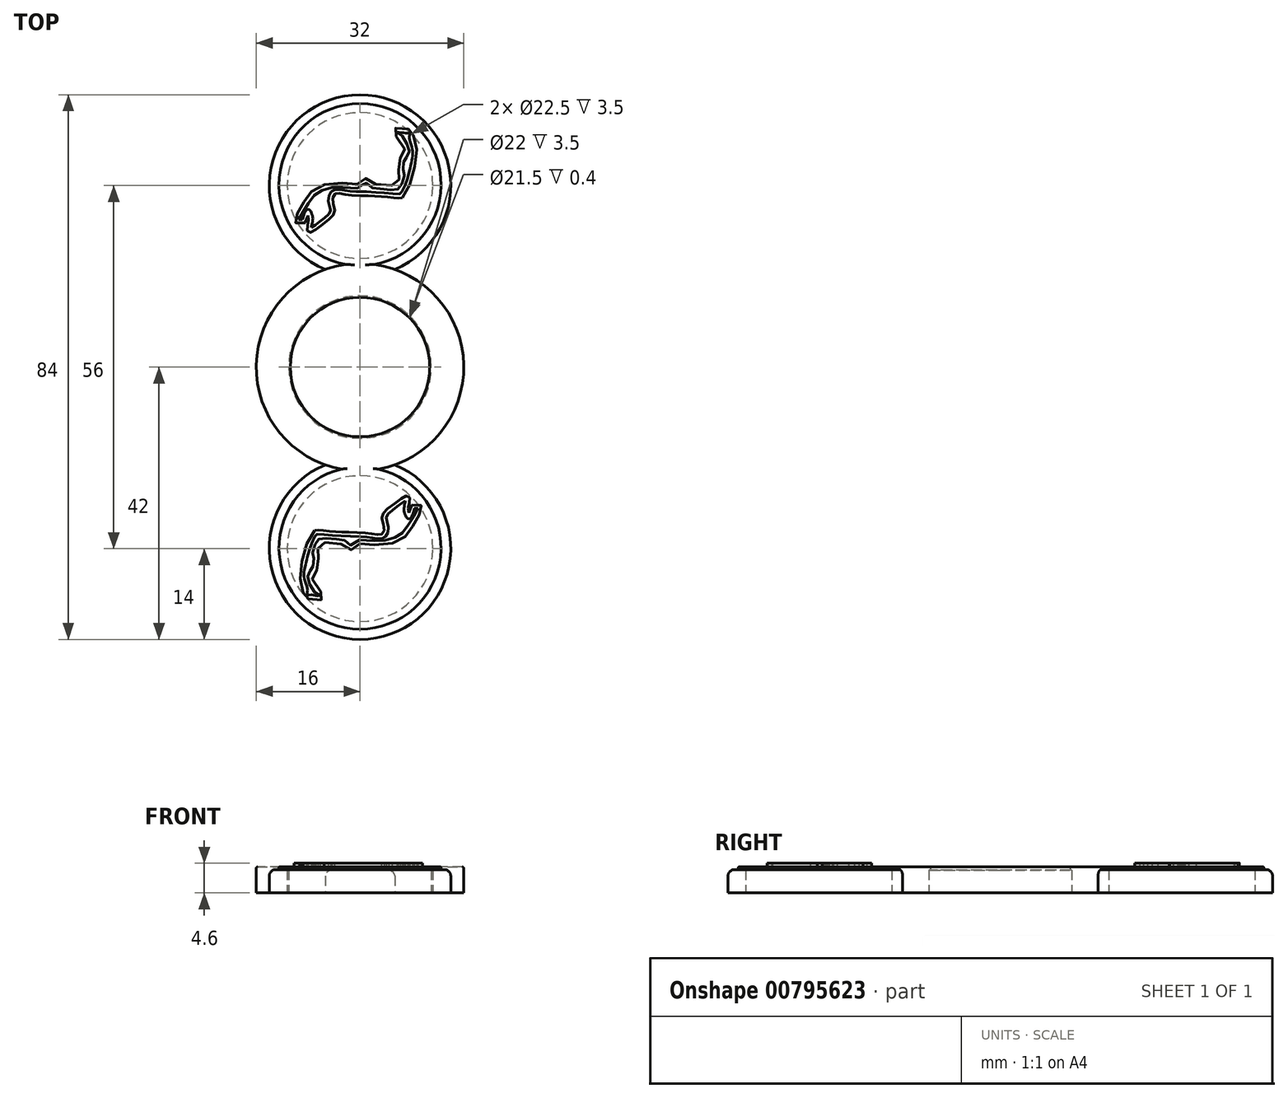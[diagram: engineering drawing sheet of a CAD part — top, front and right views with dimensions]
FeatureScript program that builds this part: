
annotation { "Feature Type Name" : "Feature", "Feature Type Description" : "" }
export const myFeature = defineFeature(function(context is Context, id is Id, definition is map)
    precondition{}
    {
        {
            var Q0;
            Q0=qCreatedBy(makeId("Top.planeOp"),FACE);
            var sketch = newSketch(context, id + "F0", { "sketchPlane" : qUnion([Q0])});
            skCircle(sketch, "E0", {"center": v(0, 0) * mm, "radius": 16 * mm});
            skCircle(sketch, "E1", {"center": v(0, 0) * mm, "radius": 11 * mm});
            skCircle(sketch, "E2", {"center": v(0, 0) * mm, "radius": 10.75 * mm});
            skCircle(sketch, "E3", {"center": v(0, 28) * mm, "radius": 14 * mm});
            skCircle(sketch, "E4", {"center": v(0, 28) * mm, "radius": 11.25 * mm});
            skCircle(sketch, "E5", {"center": v(0, 0) * mm, "radius": 40 * mm, "construction": true});
            skCircle(sketch, "E6", {"center": v(0, -28) * mm, "radius": 14 * mm});
            skCircle(sketch, "E7", {"center": v(0, -28) * mm, "radius": 11.25 * mm});
            skSolve(sketch);
        }
        {
            var Q0;
            Q0=makeQuery(id+"F0.imprint","IMPRINT",FACE,{"disambiguationData":[TD([[makeQuery(id+"F0.imprint","IMPRINT",EDGE,{"derivedFrom":sQuery(id+"F0.wireOp",EDGE,"E1")}),-1.0]])]});
            var Q1;
            {var subQ0=sQuery(id+"F0.wireOp",EDGE,"E3");var subQ1=sQuery(id+"F0.wireOp",EDGE,"E0");var subQ2=makeQuery(id+"F0.imprint","INTERSECT",VERTEX,{"disambiguationData":[OD(0.0)],"derivedFrom":[subQ1,subQ0]});Q1=makeQuery(id+"F0.imprint","IMPRINT",FACE,{"disambiguationData":[TD([[makeQuery(id+"F0.imprint","IMPRINT",EDGE,{"disambiguationData":[TD([[subQ2,1.0]])],"derivedFrom":subQ1}),1.0]])]});}
            var Q2;
            {var subQ0=sQuery(id+"F0.wireOp",EDGE,"E6");var subQ1=sQuery(id+"F0.wireOp",EDGE,"E0");var subQ2=makeQuery(id+"F0.imprint","INTERSECT",VERTEX,{"disambiguationData":[OD(0.0)],"derivedFrom":[subQ1,subQ0]});Q2=makeQuery(id+"F0.imprint","IMPRINT",FACE,{"disambiguationData":[TD([[makeQuery(id+"F0.imprint","IMPRINT",EDGE,{"disambiguationData":[TD([[subQ2,-1.0]])],"derivedFrom":subQ1}),1.0]])]});}
            extrude(context, id + "F1", {"entities" : qUnion([Q0, Q1, Q2]), "depth" : 4 * mm, "offsetDistance" : 25 * mm});
        }
        {
            var Q0;
            Q0=makeQuery(id+"F0.imprint","IMPRINT",FACE,{"disambiguationData":[TD([[makeQuery(id+"F0.imprint","IMPRINT",EDGE,{"derivedFrom":sQuery(id+"F0.wireOp",EDGE,"E1")}),1.0]])]});
            extrude(context, id + "F2", {"entities" : qUnion([Q0]), "operationType" : NewBodyOperationType.ADD, "depth" : 4 * mm, "offsetDistance" : 25 * mm, "hasSecondDirection" : true, "secondDirectionOppositeDirection" : false, "secondDirectionDepth" : 3.5 * mm});
        }
        {
            var Q0;
            Q0=makeQuery(id+"F2.opExtrude","CAP_EDGE",EDGE,{"disambiguationData":[OSD([sQuery(id+"F0.wireOp",EDGE,"E1")])],"isStart":true});
            var Q1;
            Q1=makeQuery(id+"F2.opExtrude","CAP_EDGE",EDGE,{"disambiguationData":[OSD([sQuery(id+"F0.wireOp",EDGE,"E2")])],"isStart":false});
            fillet(context, id + "F3", {"entities" : qUnion([Q0, Q1]), "radius" : 0.1 * mm, "tangentPropagation" : true, "allowEdgeOverflow" : false});
        }
        {
            var Q0;
            Q0=makeQuery(id+"F0.imprint","IMPRINT",FACE,{"disambiguationData":[TD([[makeQuery(id+"F0.imprint","IMPRINT",EDGE,{"derivedFrom":sQuery(id+"F0.wireOp",EDGE,"E7")}),-1.0]])]});
            var Q1;
            Q1=makeQuery(id+"F0.imprint","IMPRINT",FACE,{"disambiguationData":[TD([[makeQuery(id+"F0.imprint","IMPRINT",EDGE,{"derivedFrom":sQuery(id+"F0.wireOp",EDGE,"E4")}),-1.0]])]});
            extrude(context, id + "F4", {"entities" : qUnion([Q0, Q1]), "operationType" : NewBodyOperationType.ADD, "depth" : 3.6 * mm, "offsetDistance" : 25 * mm});
        }
        {
            var Q0;
            Q0=qCreatedBy(makeId("Top.planeOp"),FACE);
            var sketch = newSketch(context, id + "F5", { "sketchPlane" : qUnion([Q0])});
            skCircle(sketch, "E8", {"center": v(0, 28.15) * mm, "radius": 12.5 * mm});
            skCircle(sketch, "E9", {"center": v(0, -27.9) * mm, "radius": 12.5 * mm});
            skSolve(sketch);
        }
        {
            var Q0;
            Q0=makeQuery(id+"F5.imprint","IMPRINT",FACE,{"disambiguationData":[TD([[makeQuery(id+"F5.imprint","IMPRINT",EDGE,{"derivedFrom":sQuery(id+"F5.wireOp",EDGE,"E8")}),1.0]])]});
            var Q1;
            Q1=makeQuery(id+"F5.imprint","IMPRINT",FACE,{"disambiguationData":[TD([[makeQuery(id+"F5.imprint","IMPRINT",EDGE,{"derivedFrom":sQuery(id+"F5.wireOp",EDGE,"E9")}),1.0]])]});
            extrude(context, id + "F6", {"entities" : qUnion([Q0, Q1]), "operationType" : NewBodyOperationType.ADD, "depth" : 4 * mm, "offsetDistance" : 25 * mm, "hasSecondDirection" : true, "secondDirectionOppositeDirection" : false, "secondDirectionDepth" : 3.5 * mm});
        }
        {
            var Q0;
            Q0=makeQuery(id+"F6.boolean.opBoolean","SPLIT",EDGE,{"disambiguationData":[OD(0.0)],"derivedFrom":makeQuery(id+"F1.opExtrude","CAP_EDGE",EDGE,{"disambiguationData":[OSD([sQuery(id+"F0.wireOp",EDGE,"E0")])],"isStart":false})});
            var Q1;
            Q1=makeQuery(id+"F6.boolean.opBoolean","SPLIT",EDGE,{"disambiguationData":[OD(1.0)],"derivedFrom":makeQuery(id+"F1.opExtrude","CAP_EDGE",EDGE,{"disambiguationData":[OSD([sQuery(id+"F0.wireOp",EDGE,"E0")])],"isStart":false})});
            fillet(context, id + "F7", {"entities" : qUnion([Q0, Q1]), "radius" : 0.2 * mm, "tangentPropagation" : true, "allowEdgeOverflow" : false});
        }
        {
            var Q0;
            Q0=makeQuery(id+"F6.boolean.opBoolean","INTERSECT",EDGE,{"derivedFrom":[makeQuery(id+"F4.opExtrude","CAP_FACE",FACE,{"disambiguationData":[OSD([sQuery(id+"F0.wireOp",EDGE,"E0"),sQuery(id+"F0.wireOp",EDGE,"E6"),sQuery(id+"F0.wireOp",EDGE,"E7")])],"isStart":false}),makeQuery(id+"F6.opExtrude","SWEPT_FACE",FACE,{"disambiguationData":[OSD([sQuery(id+"F5.wireOp",EDGE,"E9")])]})]});
            var Q1;
            Q1=makeQuery(id+"F6.boolean.opBoolean","INTERSECT",EDGE,{"derivedFrom":[makeQuery(id+"F4.opExtrude","CAP_FACE",FACE,{"disambiguationData":[OSD([sQuery(id+"F0.wireOp",EDGE,"E0"),sQuery(id+"F0.wireOp",EDGE,"E3"),sQuery(id+"F0.wireOp",EDGE,"E4")])],"isStart":false}),makeQuery(id+"F6.opExtrude","SWEPT_FACE",FACE,{"disambiguationData":[OSD([sQuery(id+"F5.wireOp",EDGE,"E8")])]})]});
            fillet(context, id + "F8", {"entities" : qUnion([Q0, Q1]), "radius" : 0.2 * mm, "tangentPropagation" : true, "allowEdgeOverflow" : false});
        }
        {
            var Q0;
            Q0=makeQuery(id+"F4.opExtrude","CAP_EDGE",EDGE,{"disambiguationData":[OSD([sQuery(id+"F0.wireOp",EDGE,"E3")])],"isStart":false});
            var Q1;
            Q1=makeQuery(id+"F4.opExtrude","CAP_EDGE",EDGE,{"disambiguationData":[OSD([sQuery(id+"F0.wireOp",EDGE,"E6")])],"isStart":false});
            fillet(context, id + "F9", {"entities" : qUnion([Q0, Q1]), "radius" : 1 * mm, "tangentPropagation" : true, "allowEdgeOverflow" : false});
        }
        {
            var Q0;
            Q0=makeQuery(id+"F6.opExtrude","CAP_EDGE",EDGE,{"disambiguationData":[OSD([sQuery(id+"F5.wireOp",EDGE,"E8")])],"isStart":false});
            var Q1;
            Q1=makeQuery(id+"F6.opExtrude","CAP_EDGE",EDGE,{"disambiguationData":[OSD([sQuery(id+"F5.wireOp",EDGE,"E9")])],"isStart":false});
            fillet(context, id + "F10", {"entities" : qUnion([Q0, Q1]), "radius" : 0.1 * mm, "tangentPropagation" : true, "allowEdgeOverflow" : false});
        }
        {
            var Q0;
            Q0=qCreatedBy(makeId("Top.planeOp"),FACE);
            cPlane(context, id + "F11", {"entities" : qUnion([Q0]), "cplaneType" : CPlaneType.OFFSET, "offset" : 3.6 * mm, "width" : 150 * mm, "height" : 150 * mm});
        }
        {
            var Q0;
            Q0=qCreatedBy(id+"F11.planeOp",FACE);
            var sketch = newSketch(context, id + "F12", { "sketchPlane" : qUnion([Q0])});
            skFitSpline(sketch, "E10", {"points": [v(-7.02, -25.2) * mm, v(-6.88, -25.17) * mm, v(-6.76, -25.15) * mm, v(-6.56, -25.14) * mm, v(-6.38, -25.14) * mm, v(-6.2, -25.18) * mm, v(-5.94, -25.2) * mm, v(-5.64, -25.22) * mm, v(-5.24, -25.25) * mm, v(-4.89, -25.28) * mm, v(-4.45, -25.32) * mm, v(-4.06, -25.35) * mm, v(-3.66, -25.37) * mm, v(-3.22, -25.4) * mm, v(-2.82, -25.43) * mm, v(-2.42, -25.46) * mm, v(-1.92, -25.47) * mm, v(-1.37, -25.5) * mm, v(-0.61, -25.53) * mm, v(0.27, -25.54) * mm, v(0.81, -25.57) * mm, v(1.23, -25.61) * mm, v(1.64, -25.69) * mm, v(2.06, -25.73) * mm, v(2.43, -25.8) * mm, v(2.74, -25.87) * mm, v(2.94, -25.87) * mm, v(3.1, -25.86) * mm, v(3.28, -25.82) * mm, v(3.47, -25.72) * mm, v(3.58, -25.54) * mm, v(3.7, -25.32) * mm, v(3.77, -24.95) * mm, v(3.76, -24.57) * mm, v(3.6, -24.12) * mm, v(3.46, -23.76) * mm, v(3.39, -23.37) * mm, v(3.41, -23.12) * mm, v(3.5, -22.81) * mm, v(3.63, -22.5) * mm, v(3.76, -22.31) * mm, v(4, -22.07) * mm, v(4.49, -21.67) * mm, v(5.1, -21.22) * mm, v(5.7, -20.74) * mm, v(6.22, -20.36) * mm, v(6.74, -20.02) * mm, v(6.98, -19.9) * mm, v(7.17, -19.84) * mm, v(7.34, -19.84) * mm, v(7.5, -19.91) * mm, v(7.63, -20.08) * mm, v(7.7, -20.24) * mm, v(7.68, -20.51) * mm, v(7.6, -20.85) * mm, v(7.55, -21.15) * mm, v(7.48, -21.46) * mm, v(7.44, -21.75) * mm, v(7.42, -22.02) * mm, v(7.45, -22.33) * mm, v(7.53, -22.48) * mm], "startDerivative": vector(12.87, 4) * mm, "endDerivative": vector(8.17, -11.49) * mm});
            skFitSpline(sketch, "E11", {"points": [v(7.53, -22.48) * mm, v(7.62, -22.28) * mm, v(7.67, -22.1) * mm, v(7.71, -21.87) * mm, v(7.77, -21.65) * mm, v(7.86, -21.47) * mm, v(7.96, -21.35) * mm, v(8.11, -21.23) * mm, v(8.33, -21.2) * mm, v(8.62, -21.18) * mm, v(8.93, -21.2) * mm, v(9.21, -21.2) * mm, v(9.4, -21.3) * mm, v(9.53, -21.43) * mm, v(9.64, -21.59) * mm, v(9.64, -21.8) * mm, v(9.53, -22.09) * mm, v(9.32, -22.48) * mm, v(9.06, -22.98) * mm, v(8.81, -23.4) * mm, v(8.55, -23.86) * mm, v(8.34, -24.2) * mm, v(8.1, -24.61) * mm, v(7.87, -24.99) * mm, v(7.53, -25.52) * mm, v(7.32, -25.77) * mm, v(7.04, -26.07) * mm, v(6.6, -26.42) * mm, v(6.03, -26.79) * mm, v(5.54, -27) * mm, v(4.91, -27.2) * mm, v(4.22, -27.32) * mm, v(3.17, -27.41) * mm, v(2.14, -27.44) * mm, v(1.35, -27.4) * mm, v(0.67, -27.26) * mm, v(0.23, -27.23) * mm, v(-0.13, -27.28) * mm, v(-0.32, -27.45) * mm, v(-0.51, -27.74) * mm, v(-0.7, -27.96) * mm, v(-0.97, -28.14) * mm, v(-1.46, -28.16) * mm, v(-1.86, -27.93) * mm, v(-2.13, -27.66) * mm, v(-2.47, -27.4) * mm, v(-2.82, -27.3) * mm, v(-3.22, -27.25) * mm, v(-4, -27.17) * mm, v(-4.8, -27.11) * mm, v(-5.52, -27.05) * mm, v(-5.86, -27.03) * mm, v(-5.99, -27.06) * mm, v(-6.1, -27.16) * mm, v(-6.24, -27.37) * mm, v(-6.46, -27.89) * mm, v(-6.64, -28.4) * mm, v(-6.74, -28.78) * mm, v(-6.7, -28.97) * mm, v(-6.57, -29.18) * mm, v(-6.46, -29.38) * mm, v(-6.42, -29.63) * mm, v(-6.48, -30.12) * mm, v(-6.58, -30.56) * mm, v(-6.62, -31.03) * mm, v(-6.67, -31.33) * mm, v(-6.81, -31.64) * mm, v(-7.08, -31.86) * mm, v(-7.33, -32.02) * mm, v(-7.43, -32.13) * mm, v(-7.44, -32.42) * mm, v(-7.2, -33.1) * mm, v(-6.9, -33.83) * mm, v(-6.56, -34.3) * mm, v(-6, -34.69) * mm, v(-5.66, -34.97) * mm, v(-5.53, -35.2) * mm, v(-5.57, -35.57) * mm, v(-5.75, -35.8) * mm, v(-6.04, -35.94) * mm, v(-6.64, -35.94) * mm, v(-7.14, -35.84) * mm, v(-7.58, -35.76) * mm, v(-7.92, -35.76) * mm, v(-8.38, -35.75) * mm, v(-8.6, -35.67) * mm, v(-8.73, -35.52) * mm, v(-8.83, -35.24) * mm, v(-8.8, -34.93) * mm, v(-8.73, -34.64) * mm, v(-8.7, -34.4) * mm, v(-8.82, -33.93) * mm, v(-9.13, -33.05) * mm, v(-9.29, -32.28) * mm, v(-9.22, -31.45) * mm, v(-9.13, -30.93) * mm, v(-8.91, -29.83) * mm, v(-8.84, -29.61) * mm, v(-8.67, -28.8) * mm, v(-8.2, -27.32) * mm, v(-7.67, -26.12) * mm, v(-7.41, -25.59) * mm, v(-7.26, -25.36) * mm, v(-7.02, -25.2) * mm], "startDerivative": vector(13.18, 29.72) * mm, "endDerivative": vector(32.8, 17.75) * mm});
            skFitSpline(sketch, "E12", {"points": [v(-8.13, -29.3) * mm, v(-7.95, -28.62) * mm, v(-7.68, -27.78) * mm, v(-7.37, -26.96) * mm, v(-7.02, -26.23) * mm, v(-6.83, -25.86) * mm, v(-6.76, -25.75) * mm, v(-6.52, -25.77) * mm, v(-5.84, -25.8) * mm, v(-4.83, -25.9) * mm, v(-3.73, -25.96) * mm, v(-2.62, -26.04) * mm, v(-1.2, -26.12) * mm, v(0.33, -26.17) * mm, v(0.84, -26.2) * mm, v(1.3, -26.24) * mm, v(1.73, -26.31) * mm, v(2.16, -26.39) * mm, v(2.52, -26.46) * mm, v(2.76, -26.48) * mm, v(3.16, -26.47) * mm, v(3.46, -26.44) * mm, v(3.71, -26.33) * mm, v(3.97, -26.12) * mm, v(4.15, -25.86) * mm, v(4.3, -25.48) * mm, v(4.4, -25.02) * mm, v(4.4, -24.66) * mm, v(4.32, -24.26) * mm, v(4.19, -23.84) * mm, v(4.06, -23.56) * mm, v(4.04, -23.27) * mm, v(4.1, -22.93) * mm, v(4.25, -22.73) * mm, v(4.48, -22.48) * mm, v(4.89, -22.17) * mm, v(5.33, -21.8) * mm, v(5.73, -21.52) * mm, v(6.17, -21.17) * mm, v(6.46, -20.94) * mm, v(6.77, -20.73) * mm, v(6.99, -20.6) * mm], "startDerivative": vector(5.81, 22.58) * mm, "endDerivative": vector(11.7, 7.1) * mm});
            skFitSpline(sketch, "E13", {"points": [v(6.99, -20.6) * mm, v(6.99, -20.86) * mm, v(6.88, -21.18) * mm, v(6.82, -21.54) * mm, v(6.78, -21.9) * mm, v(6.8, -22.22) * mm, v(6.87, -22.48) * mm, v(6.99, -22.83) * mm, v(7.11, -23.11) * mm, v(7.23, -23.27) * mm, v(7.4, -23.37) * mm, v(7.62, -23.38) * mm, v(7.79, -23.28) * mm, v(7.94, -23.11) * mm, v(8.1, -22.76) * mm, v(8.2, -22.48) * mm, v(8.28, -22.17) * mm, v(8.37, -21.87) * mm, v(8.4, -21.8) * mm], "startDerivative": vector(0.5, -4.8) * mm, "endDerivative": vector(0.7, 2) * mm});
            skFitSpline(sketch, "E14", {"points": [v(8.4, -21.8) * mm, v(8.96, -21.8) * mm], "startDerivative": vector(0.57, 0) * mm, "endDerivative": vector(0.57, 0) * mm});
            skFitSpline(sketch, "E15", {"points": [v(8.96, -21.8) * mm, v(8.67, -22.31) * mm, v(8.4, -22.82) * mm, v(8, -23.51) * mm, v(7.53, -24.19) * mm, v(7.12, -24.86) * mm, v(6.65, -25.5) * mm, v(6.4, -25.71) * mm, v(5.87, -26.05) * mm, v(5.22, -26.38) * mm, v(4.45, -26.63) * mm, v(3.7, -26.76) * mm, v(2.93, -26.8) * mm, v(1.91, -26.79) * mm, v(1.44, -26.79) * mm, v(1.15, -26.73) * mm, v(0.78, -26.65) * mm, v(0.34, -26.64) * mm, v(0, -26.64) * mm, v(-0.24, -26.68) * mm, v(-0.51, -26.79) * mm, v(-0.7, -26.92) * mm, v(-0.85, -27.16) * mm, v(-0.99, -27.37) * mm, v(-1.16, -27.54) * mm, v(-1.35, -27.55) * mm, v(-1.66, -27.28) * mm, v(-2.05, -26.9) * mm, v(-2.32, -26.75) * mm, v(-2.73, -26.64) * mm, v(-3.26, -26.58) * mm, v(-3.7, -26.54) * mm, v(-4.56, -26.48) * mm, v(-5.4, -26.4) * mm, v(-5.99, -26.39) * mm, v(-6.2, -26.44) * mm, v(-6.4, -26.56) * mm, v(-6.57, -26.7) * mm, v(-6.73, -26.93) * mm, v(-6.97, -27.47) * mm, v(-7.16, -28.05) * mm, v(-7.3, -28.5) * mm, v(-7.34, -28.89) * mm, v(-7.3, -29.08) * mm, v(-7.2, -29.35) * mm, v(-7.12, -29.64) * mm, v(-7.19, -30.1) * mm, v(-7.2, -30.54) * mm, v(-7.23, -30.93) * mm, v(-7.26, -31.16) * mm, v(-7.45, -31.3) * mm, v(-7.7, -31.45) * mm, v(-7.95, -31.7) * mm, v(-8.07, -32.02) * mm, v(-8.08, -32.4) * mm, v(-8, -32.74) * mm, v(-7.86, -33.18) * mm, v(-7.56, -33.92) * mm, v(-7.23, -34.46) * mm, v(-6.97, -34.76) * mm, v(-6.71, -34.95) * mm, v(-6.34, -35.16) * mm, v(-6.18, -35.26) * mm], "startDerivative": vector(-15.7, -27.99) * mm, "endDerivative": vector(12.87, -8.44) * mm});
            skFitSpline(sketch, "E16", {"points": [v(-6.18, -35.26) * mm, v(-6.75, -35.26) * mm, v(-7.25, -35.18) * mm, v(-7.73, -35.13) * mm, v(-8.18, -35.14) * mm, v(-8.14, -34.82) * mm, v(-8.1, -34.56) * mm, v(-8.12, -34.23) * mm, v(-8.22, -33.8) * mm, v(-8.43, -33.18) * mm, v(-8.61, -32.53) * mm, v(-8.65, -32.03) * mm, v(-8.59, -31.45) * mm, v(-8.48, -30.9) * mm, v(-8.3, -30.07) * mm, v(-8.13, -29.3) * mm], "startDerivative": vector(-8.3, -0.53) * mm, "endDerivative": vector(2, 9.14) * mm});
            skFitSpline(sketch, "E17", {"points": [v(6.52, 26.13) * mm, v(6.39, 26.1) * mm, v(6.27, 26.08) * mm, v(6.06, 26.07) * mm, v(5.88, 26.07) * mm, v(5.71, 26.1) * mm, v(5.45, 26.13) * mm, v(5.14, 26.14) * mm, v(4.75, 26.18) * mm, v(4.4, 26.2) * mm, v(3.96, 26.25) * mm, v(3.56, 26.28) * mm, v(3.16, 26.3) * mm, v(2.73, 26.34) * mm, v(2.33, 26.36) * mm, v(1.93, 26.38) * mm, v(1.42, 26.4) * mm, v(0.88, 26.43) * mm, v(0.12, 26.46) * mm, v(-0.76, 26.47) * mm, v(-1.3, 26.5) * mm, v(-1.72, 26.54) * mm, v(-2.13, 26.61) * mm, v(-2.55, 26.66) * mm, v(-2.93, 26.73) * mm, v(-3.23, 26.8) * mm, v(-3.44, 26.8) * mm, v(-3.6, 26.78) * mm, v(-3.77, 26.75) * mm, v(-3.97, 26.65) * mm, v(-4.08, 26.47) * mm, v(-4.18, 26.25) * mm, v(-4.27, 25.88) * mm, v(-4.26, 25.5) * mm, v(-4.09, 25.04) * mm, v(-3.96, 24.7) * mm, v(-3.88, 24.3) * mm, v(-3.9, 24.05) * mm, v(-4, 23.74) * mm, v(-4.12, 23.44) * mm, v(-4.26, 23.24) * mm, v(-4.49, 23) * mm, v(-4.98, 22.6) * mm, v(-5.59, 22.14) * mm, v(-6.2, 21.67) * mm, v(-6.71, 21.28) * mm, v(-7.23, 20.95) * mm, v(-7.47, 20.83) * mm, v(-7.66, 20.77) * mm, v(-7.83, 20.77) * mm, v(-8, 20.84) * mm, v(-8.12, 21) * mm, v(-8.18, 21.16) * mm, v(-8.17, 21.44) * mm, v(-8.1, 21.78) * mm, v(-8.04, 22.08) * mm, v(-7.98, 22.38) * mm, v(-7.93, 22.67) * mm, v(-7.92, 22.95) * mm, v(-7.94, 23.25) * mm, v(-8.03, 23.41) * mm], "startDerivative": vector(-12.87, -4) * mm, "endDerivative": vector(-8.17, 11.49) * mm});
            skFitSpline(sketch, "E18", {"points": [v(-8.03, 23.41) * mm, v(-8.11, 23.2) * mm, v(-8.16, 23.03) * mm, v(-8.2, 22.8) * mm, v(-8.27, 22.58) * mm, v(-8.35, 22.4) * mm, v(-8.45, 22.28) * mm, v(-8.6, 22.15) * mm, v(-8.83, 22.12) * mm, v(-9.12, 22.1) * mm, v(-9.43, 22.12) * mm, v(-9.7, 22.13) * mm, v(-9.89, 22.23) * mm, v(-10.02, 22.36) * mm, v(-10.13, 22.52) * mm, v(-10.13, 22.74) * mm, v(-10.02, 23.01) * mm, v(-9.82, 23.41) * mm, v(-9.55, 23.9) * mm, v(-9.3, 24.33) * mm, v(-9.04, 24.79) * mm, v(-8.84, 25.13) * mm, v(-8.6, 25.54) * mm, v(-8.37, 25.91) * mm, v(-8.03, 26.44) * mm, v(-7.8, 26.7) * mm, v(-7.53, 27) * mm, v(-7.1, 27.35) * mm, v(-6.53, 27.71) * mm, v(-6.03, 27.92) * mm, v(-5.4, 28.14) * mm, v(-4.72, 28.25) * mm, v(-3.67, 28.34) * mm, v(-2.64, 28.37) * mm, v(-1.84, 28.32) * mm, v(-1.16, 28.18) * mm, v(-0.73, 28.16) * mm, v(-0.37, 28.2) * mm, v(-0.17, 28.38) * mm, v(0.02, 28.67) * mm, v(0.21, 28.89) * mm, v(0.48, 29.07) * mm, v(0.96, 29.1) * mm, v(1.36, 28.86) * mm, v(1.64, 28.58) * mm, v(1.98, 28.32) * mm, v(2.33, 28.22) * mm, v(2.73, 28.17) * mm, v(3.51, 28.1) * mm, v(4.3, 28.04) * mm, v(5.02, 27.98) * mm, v(5.36, 27.96) * mm, v(5.5, 28) * mm, v(5.62, 28.09) * mm, v(5.75, 28.3) * mm, v(5.97, 28.81) * mm, v(6.15, 29.33) * mm, v(6.24, 29.7) * mm, v(6.2, 29.9) * mm, v(6.07, 30.1) * mm, v(5.97, 30.31) * mm, v(5.93, 30.55) * mm, v(5.99, 31.05) * mm, v(6.09, 31.48) * mm, v(6.12, 31.96) * mm, v(6.17, 32.26) * mm, v(6.32, 32.57) * mm, v(6.58, 32.79) * mm, v(6.84, 32.95) * mm, v(6.93, 33.05) * mm, v(6.94, 33.34) * mm, v(6.72, 34.03) * mm, v(6.4, 34.76) * mm, v(6.06, 35.22) * mm, v(5.5, 35.62) * mm, v(5.17, 35.9) * mm, v(5.04, 36.14) * mm, v(5.07, 36.5) * mm, v(5.25, 36.73) * mm, v(5.54, 36.86) * mm, v(6.15, 36.86) * mm, v(6.64, 36.76) * mm, v(7.09, 36.7) * mm, v(7.43, 36.7) * mm, v(7.89, 36.68) * mm, v(8.1, 36.6) * mm, v(8.24, 36.45) * mm, v(8.33, 36.17) * mm, v(8.31, 35.86) * mm, v(8.24, 35.57) * mm, v(8.2, 35.33) * mm, v(8.32, 34.86) * mm, v(8.64, 33.97) * mm, v(8.8, 33.21) * mm, v(8.72, 32.38) * mm, v(8.64, 31.86) * mm, v(8.42, 30.76) * mm, v(8.35, 30.54) * mm, v(8.18, 29.73) * mm, v(7.7, 28.25) * mm, v(7.17, 27.05) * mm, v(6.92, 26.52) * mm, v(6.76, 26.29) * mm, v(6.52, 26.13) * mm], "startDerivative": vector(-13.18, -29.72) * mm, "endDerivative": vector(-32.8, -17.75) * mm});
            skFitSpline(sketch, "E19", {"points": [v(7.63, 30.23) * mm, v(7.45, 29.55) * mm, v(7.19, 28.7) * mm, v(6.87, 27.88) * mm, v(6.52, 27.16) * mm, v(6.34, 26.78) * mm, v(6.27, 26.67) * mm, v(6.03, 26.7) * mm, v(5.35, 26.73) * mm, v(4.33, 26.82) * mm, v(3.23, 26.9) * mm, v(2.12, 26.96) * mm, v(0.7, 27.05) * mm, v(-0.83, 27.1) * mm, v(-1.33, 27.12) * mm, v(-1.8, 27.17) * mm, v(-2.23, 27.24) * mm, v(-2.65, 27.31) * mm, v(-3.01, 27.39) * mm, v(-3.25, 27.41) * mm, v(-3.65, 27.4) * mm, v(-3.96, 27.36) * mm, v(-4.2, 27.25) * mm, v(-4.46, 27.05) * mm, v(-4.64, 26.78) * mm, v(-4.79, 26.4) * mm, v(-4.9, 25.95) * mm, v(-4.89, 25.59) * mm, v(-4.81, 25.19) * mm, v(-4.68, 24.77) * mm, v(-4.56, 24.49) * mm, v(-4.54, 24.2) * mm, v(-4.6, 23.86) * mm, v(-4.74, 23.65) * mm, v(-4.97, 23.41) * mm, v(-5.38, 23.1) * mm, v(-5.83, 22.74) * mm, v(-6.23, 22.44) * mm, v(-6.66, 22.1) * mm, v(-6.95, 21.86) * mm, v(-7.27, 21.66) * mm, v(-7.48, 21.53) * mm], "startDerivative": vector(-5.81, -22.58) * mm, "endDerivative": vector(-11.7, -7.1) * mm});
            skFitSpline(sketch, "E20", {"points": [v(-7.48, 21.53) * mm, v(-7.48, 21.8) * mm, v(-7.37, 22.1) * mm, v(-7.31, 22.47) * mm, v(-7.28, 22.82) * mm, v(-7.3, 23.15) * mm, v(-7.36, 23.41) * mm, v(-7.48, 23.76) * mm, v(-7.6, 24.04) * mm, v(-7.73, 24.2) * mm, v(-7.9, 24.3) * mm, v(-8.11, 24.3) * mm, v(-8.28, 24.2) * mm, v(-8.44, 24.04) * mm, v(-8.6, 23.69) * mm, v(-8.7, 23.41) * mm, v(-8.78, 23.1) * mm, v(-8.86, 22.8) * mm, v(-8.89, 22.72) * mm], "startDerivative": vector(-0.5, 4.8) * mm, "endDerivative": vector(-0.7, -2) * mm});
            skFitSpline(sketch, "E21", {"points": [v(-8.89, 22.72) * mm, v(-9.45, 22.72) * mm], "startDerivative": vector(-0.57, 0) * mm, "endDerivative": vector(-0.57, 0) * mm});
            skFitSpline(sketch, "E22", {"points": [v(-9.45, 22.72) * mm, v(-9.16, 23.24) * mm, v(-8.89, 23.75) * mm, v(-8.49, 24.44) * mm, v(-8.03, 25.12) * mm, v(-7.62, 25.8) * mm, v(-7.15, 26.42) * mm, v(-6.9, 26.64) * mm, v(-6.36, 26.98) * mm, v(-5.72, 27.3) * mm, v(-4.95, 27.56) * mm, v(-4.2, 27.69) * mm, v(-3.42, 27.73) * mm, v(-2.4, 27.71) * mm, v(-1.94, 27.71) * mm, v(-1.65, 27.65) * mm, v(-1.27, 27.58) * mm, v(-0.84, 27.57) * mm, v(-0.5, 27.57) * mm, v(-0.26, 27.6) * mm, v(0.02, 27.71) * mm, v(0.2, 27.85) * mm, v(0.36, 28.09) * mm, v(0.5, 28.3) * mm, v(0.66, 28.46) * mm, v(0.85, 28.47) * mm, v(1.17, 28.2) * mm, v(1.56, 27.83) * mm, v(1.82, 27.68) * mm, v(2.23, 27.57) * mm, v(2.76, 27.5) * mm, v(3.21, 27.47) * mm, v(4.07, 27.41) * mm, v(4.9, 27.33) * mm, v(5.5, 27.31) * mm, v(5.7, 27.36) * mm, v(5.9, 27.48) * mm, v(6.07, 27.63) * mm, v(6.23, 27.86) * mm, v(6.48, 28.4) * mm, v(6.67, 28.98) * mm, v(6.8, 29.43) * mm, v(6.85, 29.82) * mm, v(6.81, 30) * mm, v(6.7, 30.28) * mm, v(6.63, 30.57) * mm, v(6.7, 31.04) * mm, v(6.72, 31.47) * mm, v(6.74, 31.86) * mm, v(6.76, 32.09) * mm, v(6.96, 32.22) * mm, v(7.21, 32.38) * mm, v(7.45, 32.63) * mm, v(7.57, 32.95) * mm, v(7.59, 33.32) * mm, v(7.51, 33.67) * mm, v(7.37, 34.1) * mm, v(7.07, 34.84) * mm, v(6.74, 35.39) * mm, v(6.48, 35.69) * mm, v(6.22, 35.88) * mm, v(5.84, 36.09) * mm, v(5.69, 36.18) * mm], "startDerivative": vector(15.7, 27.99) * mm, "endDerivative": vector(-12.87, 8.44) * mm});
            skFitSpline(sketch, "E23", {"points": [v(5.69, 36.18) * mm, v(6.26, 36.18) * mm, v(6.76, 36.1) * mm, v(7.23, 36.06) * mm, v(7.68, 36.06) * mm, v(7.65, 35.75) * mm, v(7.6, 35.48) * mm, v(7.62, 35.16) * mm, v(7.73, 34.73) * mm, v(7.94, 34.1) * mm, v(8.12, 33.45) * mm, v(8.15, 32.96) * mm, v(8.1, 32.38) * mm, v(7.98, 31.83) * mm, v(7.8, 31) * mm, v(7.63, 30.23) * mm], "startDerivative": vector(8.3, 0.53) * mm, "endDerivative": vector(-2, -9.14) * mm});
            skSolve(sketch);
        }
        {
            var Q0;
            Q0 = qSketchRegion(id + "F12", true);
            extrude(context, id + "F13", {"entities" : qUnion([Q0]), "operationType" : NewBodyOperationType.ADD, "depth" : 1 * mm, "offsetDistance" : 25 * mm});
        }
    });
